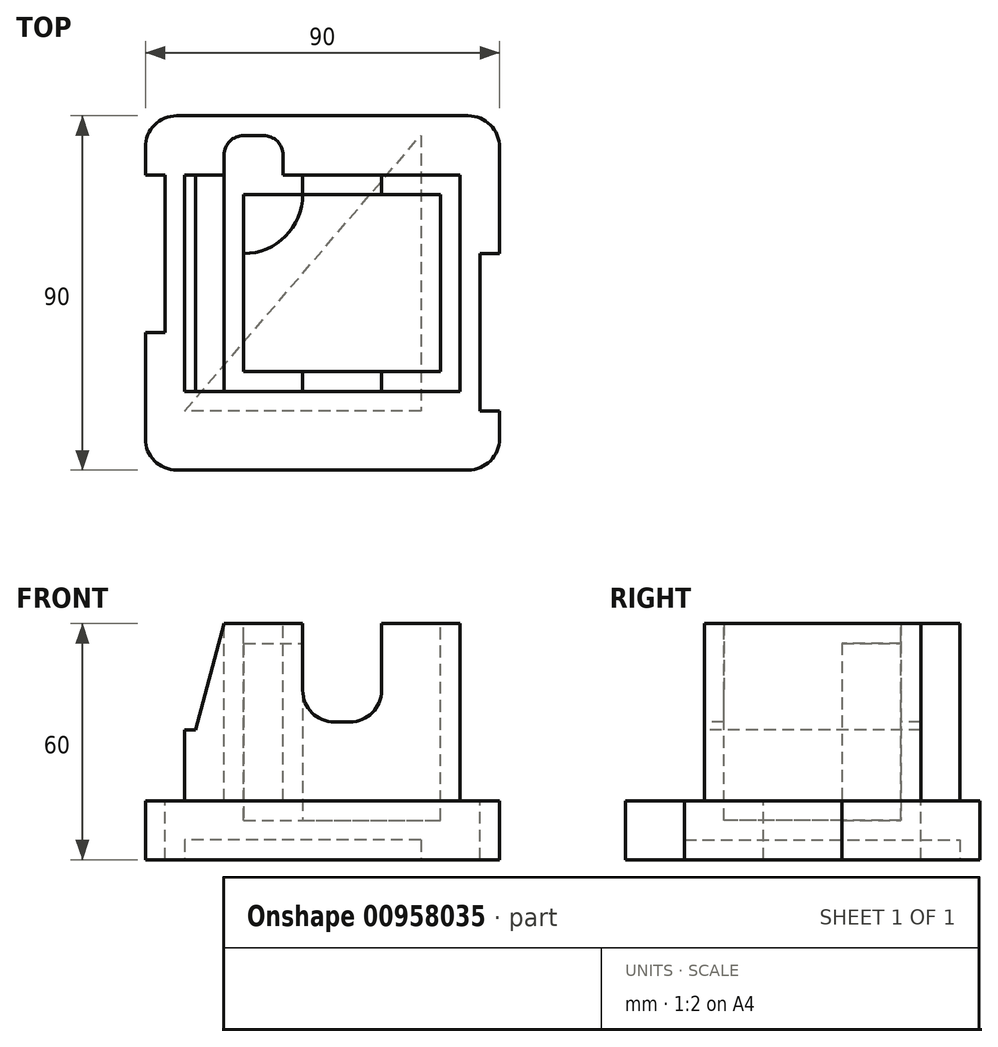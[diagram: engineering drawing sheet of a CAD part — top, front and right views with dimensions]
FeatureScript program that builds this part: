
annotation { "Feature Type Name" : "Feature", "Feature Type Description" : "" }
export const myFeature = defineFeature(function(context is Context, id is Id, definition is map)
    precondition{}
    {
        {
            var Q0;
            Q0=qCreatedBy(makeId("Front.planeOp"),FACE);
            var sketch = newSketch(context, id + "F0", { "sketchPlane" : qUnion([Q0])});
            skLineSegment(sketch, "E0", {"start": v(0, 0) * mm, "end": v(0, 18) * mm});
            skLineSegment(sketch, "E1", {"start": v(0, 18) * mm, "end": v(2.77, 18) * mm});
            skLineSegment(sketch, "E2", {"start": v(2.77, 18) * mm, "end": v(10, 45) * mm});
            skLineSegment(sketch, "E3", {"start": v(10, 45) * mm, "end": v(30, 45) * mm});
            skLineSegment(sketch, "E4", {"start": v(30, 45) * mm, "end": v(30, 20) * mm});
            skLineSegment(sketch, "E5", {"start": v(30, 20) * mm, "end": v(50, 20) * mm});
            skLineSegment(sketch, "E6", {"start": v(50, 20) * mm, "end": v(50, 45) * mm});
            skLineSegment(sketch, "E7", {"start": v(50, 45) * mm, "end": v(70, 45) * mm});
            skLineSegment(sketch, "E8", {"start": v(70, 45) * mm, "end": v(70, 0) * mm});
            skLineSegment(sketch, "E9", {"start": v(70, 0) * mm, "end": v(0, 0) * mm});
            skLineSegment(sketch, "E10", {"start": v(10, 45) * mm, "end": v(10, 0) * mm, "construction": true});
            skSolve(sketch);
        }
        {
            var Q0;
            Q0 = qSketchRegion(id + "F0", true);
            extrude(context, id + "F1", {"entities" : qUnion([Q0]), "oppositeDirection" : true, "depth" : 55 * mm, "offsetDistance" : 25 * mm});
        }
        {
            var Q0;
            Q0=makeQuery(id+"F1.opExtrude","SWEPT_EDGE",EDGE,{"disambiguationData":[OSD([sQuery(id+"F0.wireOp",EDGE,"E4"),sQuery(id+"F0.wireOp",EDGE,"E5")])]});
            var Q1;
            Q1=makeQuery(id+"F1.opExtrude","SWEPT_EDGE",EDGE,{"disambiguationData":[OSD([sQuery(id+"F0.wireOp",EDGE,"E5"),sQuery(id+"F0.wireOp",EDGE,"E6")])]});
            fillet(context, id + "F2", {"entities" : qUnion([Q0, Q1]), "radius" : 8 * mm, "tangentPropagation" : true, "allowEdgeOverflow" : false});
        }
        {
            var Q0;
            Q0=makeQuery(id+"F1.opExtrude","SWEPT_FACE",FACE,{"disambiguationData":[OSD([sQuery(id+"F0.wireOp",EDGE,"E9")])]});
            var sketch = newSketch(context, id + "F3", { "sketchPlane" : qUnion([Q0])});
            skLineSegment(sketch, "E11.bottom", {"start": v(-10, -70) * mm, "end": v(80, -70) * mm});
            skLineSegment(sketch, "E11.top", {"start": v(-10, 20) * mm, "end": v(80, 20) * mm});
            skLineSegment(sketch, "E11.left", {"start": v(-10, -70) * mm, "end": v(-10, 20) * mm});
            skLineSegment(sketch, "E11.right", {"start": v(80, -70) * mm, "end": v(80, 20) * mm});
            skSolve(sketch);
        }
        {
            var Q0;
            Q0 = qSketchRegion(id + "F3", true);
            extrude(context, id + "F4", {"entities" : qUnion([Q0]), "operationType" : NewBodyOperationType.ADD, "depth" : 15 * mm, "offsetDistance" : 25 * mm});
        }
        {
            var Q0;
            Q0=makeQuery(id+"F4.opExtrude","SWEPT_EDGE",EDGE,{"disambiguationData":[OSD([sQuery(id+"F3.wireOp",EDGE,"E11.top"),sQuery(id+"F3.wireOp",EDGE,"E11.left")])]});
            var Q1;
            Q1=makeQuery(id+"F4.opExtrude","SWEPT_EDGE",EDGE,{"disambiguationData":[OSD([sQuery(id+"F3.wireOp",EDGE,"E11.top"),sQuery(id+"F3.wireOp",EDGE,"E11.right")])]});
            var Q2;
            Q2=makeQuery(id+"F4.opExtrude","SWEPT_EDGE",EDGE,{"disambiguationData":[OSD([sQuery(id+"F3.wireOp",EDGE,"E11.bottom"),sQuery(id+"F3.wireOp",EDGE,"E11.left")])]});
            var Q3;
            Q3=makeQuery(id+"F4.opExtrude","SWEPT_EDGE",EDGE,{"disambiguationData":[OSD([sQuery(id+"F3.wireOp",EDGE,"E11.bottom"),sQuery(id+"F3.wireOp",EDGE,"E11.right")])]});
            fillet(context, id + "F5", {"entities" : qUnion([Q0, Q1, Q2, Q3]), "radius" : 8 * mm, "tangentPropagation" : true, "allowEdgeOverflow" : false});
        }
        {
            var Q0;
            Q0=makeQuery(id+"F1.opExtrude","SWEPT_FACE",FACE,{"disambiguationData":[OSD([sQuery(id+"F0.wireOp",EDGE,"E3")])]});
            var sketch = newSketch(context, id + "F6", { "sketchPlane" : qUnion([Q0])});
            skLineSegment(sketch, "E12.bottom", {"start": v(10, 55) * mm, "end": v(25, 55) * mm});
            skLineSegment(sketch, "E12.top", {"start": v(10, 65) * mm, "end": v(25, 65) * mm});
            skLineSegment(sketch, "E12.left", {"start": v(10, 55) * mm, "end": v(10, 65) * mm});
            skLineSegment(sketch, "E12.right", {"start": v(25, 55) * mm, "end": v(25, 65) * mm});
            skSolve(sketch);
        }
        {
            var Q0;
            Q0 = qSketchRegion(id + "F6", true);
            extrude(context, id + "F7", {"entities" : qUnion([Q0]), "operationType" : NewBodyOperationType.ADD, "endBound" : BoundingType.UP_TO_NEXT, "oppositeDirection" : true, "depth" : 25 * mm, "offsetDistance" : 25 * mm});
        }
        {
            var Q0;
            Q0=makeQuery(id+"F7.opExtrude","SWEPT_EDGE",EDGE,{"disambiguationData":[OSD([sQuery(id+"F6.wireOp",EDGE,"E12.top"),sQuery(id+"F6.wireOp",EDGE,"E12.left")])]});
            var Q1;
            Q1=makeQuery(id+"F7.opExtrude","SWEPT_EDGE",EDGE,{"disambiguationData":[OSD([sQuery(id+"F6.wireOp",EDGE,"E12.top"),sQuery(id+"F6.wireOp",EDGE,"E12.right")])]});
            fillet(context, id + "F8", {"entities" : qUnion([Q0, Q1]), "radius" : 5 * mm, "tangentPropagation" : true, "allowEdgeOverflow" : false});
        }
        {
            var Q0;
            Q0=makeQuery(id+"F7.boolean.opBoolean","MERGE",FACE,{"derivedFrom":[makeQuery(id+"F1.opExtrude","SWEPT_FACE",FACE,{"disambiguationData":[OSD([sQuery(id+"F0.wireOp",EDGE,"E3")])]}),makeQuery(id+"F7.opExtrude","CAP_FACE",FACE,{"disambiguationData":[OSD([sQuery(id+"F6.wireOp",EDGE,"E12.bottom"),sQuery(id+"F6.wireOp",EDGE,"E12.top"),sQuery(id+"F6.wireOp",EDGE,"E12.left"),sQuery(id+"F6.wireOp",EDGE,"E12.right")])],"isStart":true})]});
            var sketch = newSketch(context, id + "F9", { "sketchPlane" : qUnion([Q0])});
            skLineSegment(sketch, "E13.bottom", {"start": v(15, 50) * mm, "end": v(65, 50) * mm});
            skLineSegment(sketch, "E13.top", {"start": v(15, 5) * mm, "end": v(65, 5) * mm});
            skLineSegment(sketch, "E13.left", {"start": v(15, 50) * mm, "end": v(15, 5) * mm});
            skLineSegment(sketch, "E13.right", {"start": v(65, 50) * mm, "end": v(65, 5) * mm});
            skSolve(sketch);
        }
        {
            var Q0;
            Q0 = qSketchRegion(id + "F9", true);
            extrude(context, id + "F10", {"entities" : qUnion([Q0]), "operationType" : NewBodyOperationType.REMOVE, "oppositeDirection" : true, "depth" : 50 * mm, "offsetDistance" : 25 * mm});
        }
        {
            var Q0;
            Q0=makeQuery(id+"F10.boolean.opBoolean","COPY",FACE,{"derivedFrom":makeQuery(id+"F10.opExtrude","CAP_FACE",FACE,{"disambiguationData":[OSD([sQuery(id+"F9.wireOp",EDGE,"E13.bottom"),sQuery(id+"F9.wireOp",EDGE,"E13.top"),sQuery(id+"F9.wireOp",EDGE,"E13.left"),sQuery(id+"F9.wireOp",EDGE,"E13.right")])],"isStart":false})});
            var sketch = newSketch(context, id + "F11", { "sketchPlane" : qUnion([Q0])});
            skLineSegment(sketch, "E14", {"start": v(30, 50) * mm, "end": v(15, 50) * mm});
            skLineSegment(sketch, "E15", {"start": v(15, 50) * mm, "end": v(15, 35) * mm});
            skArc(sketch, "E16", {"start": v(15, 35) * mm, "mid": v(25.6, 39.4) * mm, "end": v(30, 50) * mm});
            skSolve(sketch);
        }
        {
            var Q0;
            Q0 = qSketchRegion(id + "F11", true);
            extrude(context, id + "F12", {"entities" : qUnion([Q0]), "operationType" : NewBodyOperationType.ADD, "depth" : 45 * mm, "offsetDistance" : 25 * mm});
        }
        {
            var Q0;
            Q0=makeQuery(id+"F4.opExtrude","CAP_FACE",FACE,{"disambiguationData":[OSD([sQuery(id+"F3.wireOp",EDGE,"E11.bottom"),sQuery(id+"F3.wireOp",EDGE,"E11.top"),sQuery(id+"F3.wireOp",EDGE,"E11.left"),sQuery(id+"F3.wireOp",EDGE,"E11.right")])],"isStart":true});
            var sketch = newSketch(context, id + "F13", { "sketchPlane" : qUnion([Q0])});
            skLineSegment(sketch, "E17.bottom", {"start": v(-10, 55) * mm, "end": v(-5, 55) * mm});
            skLineSegment(sketch, "E17.top", {"start": v(-10, 15) * mm, "end": v(-5, 15) * mm});
            skLineSegment(sketch, "E17.left", {"start": v(-10, 55) * mm, "end": v(-10, 15) * mm});
            skLineSegment(sketch, "E17.right", {"start": v(-5, 55) * mm, "end": v(-5, 15) * mm});
            skLineSegment(sketch, "E18.bottom", {"start": v(80, 35) * mm, "end": v(75, 35) * mm});
            skLineSegment(sketch, "E18.top", {"start": v(80, -5) * mm, "end": v(75, -5) * mm});
            skLineSegment(sketch, "E18.left", {"start": v(80, 35) * mm, "end": v(80, -5) * mm});
            skLineSegment(sketch, "E18.right", {"start": v(75, 35) * mm, "end": v(75, -5) * mm});
            skSolve(sketch);
        }
        {
            var Q0;
            Q0 = qSketchRegion(id + "F13", true);
            extrude(context, id + "F14", {"entities" : qUnion([Q0]), "operationType" : NewBodyOperationType.REMOVE, "endBound" : BoundingType.THROUGH_ALL, "oppositeDirection" : true, "depth" : 25 * mm, "offsetDistance" : 25 * mm});
        }
        {
            var Q0;
            Q0=makeQuery(id+"F4.opExtrude","CAP_FACE",FACE,{"disambiguationData":[OSD([sQuery(id+"F3.wireOp",EDGE,"E11.bottom"),sQuery(id+"F3.wireOp",EDGE,"E11.top"),sQuery(id+"F3.wireOp",EDGE,"E11.left"),sQuery(id+"F3.wireOp",EDGE,"E11.right")])],"isStart":false});
            var sketch = newSketch(context, id + "F15", { "sketchPlane" : qUnion([Q0])});
            skLineSegment(sketch, "E19", {"start": v(0, 5) * mm, "end": v(60, -65) * mm});
            skLineSegment(sketch, "E20", {"start": v(60, -65) * mm, "end": v(60, 5) * mm});
            skLineSegment(sketch, "E21", {"start": v(60, 5) * mm, "end": v(0, 5) * mm});
            skSolve(sketch);
        }
        {
            var Q0;
            Q0 = qSketchRegion(id + "F15", true);
            extrude(context, id + "F16", {"entities" : qUnion([Q0]), "operationType" : NewBodyOperationType.REMOVE, "oppositeDirection" : true, "depth" : 5 * mm, "offsetDistance" : 25 * mm});
        }
    });
